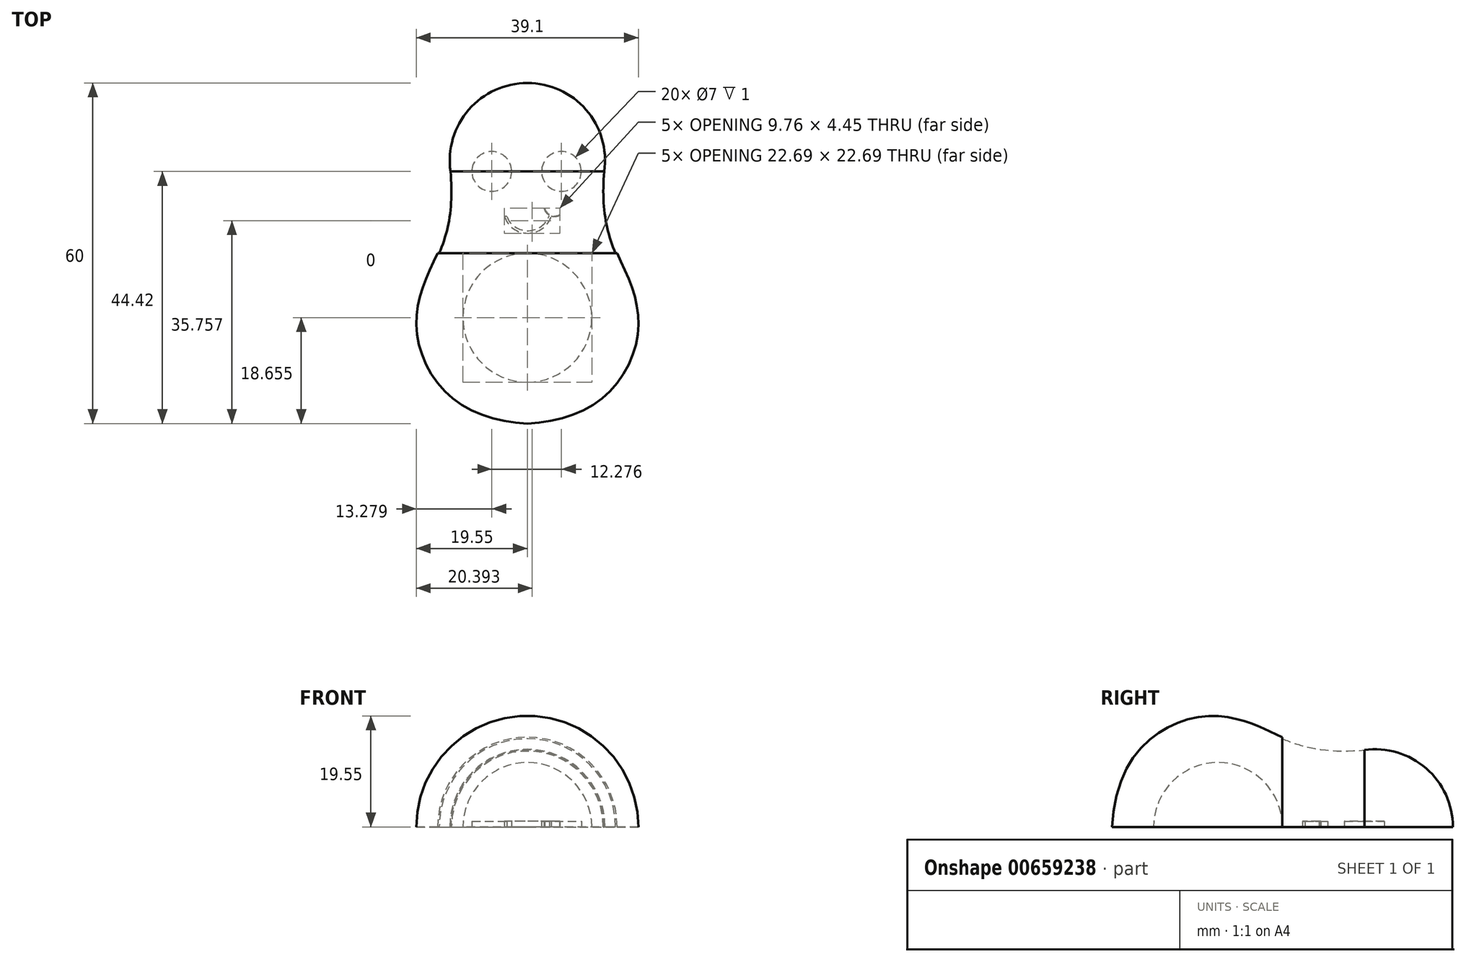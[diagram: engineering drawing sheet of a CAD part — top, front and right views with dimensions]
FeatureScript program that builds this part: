
annotation { "Feature Type Name" : "Feature", "Feature Type Description" : "" }
export const myFeature = defineFeature(function(context is Context, id is Id, definition is map)
    precondition{}
    {
        {
            var Q0;
            Q0=qCreatedBy(makeId("Top.planeOp"),FACE);
            var sketch = newSketch(context, id + "F0", { "sketchPlane" : qUnion([Q0])});
            skArc(sketch, "E0", {"start": v(13.54, 0) * mm, "mid": v(0, 15.58) * mm, "end": v(-13.54, 0) * mm});
            skFitSpline(sketch, "E1", {"points": [v(13.54, 0) * mm, v(14.1, -9.9) * mm, v(17.71, -18.6) * mm, v(19.44, -28.62) * mm, v(13.54, -39.68) * mm, v(0, -44.42) * mm, v(-13.72, -40.7) * mm, v(-20.09, -28.62) * mm, v(-17.3, -18.38) * mm, v(-14.11, -10.2) * mm, v(-13.54, 0) * mm], "startDerivative": vector(5.18, -120.5) * mm, "endDerivative": vector(-10.42, 118.7) * mm});
            skLineSegment(sketch, "E2", {"start": v(0, 15.58) * mm, "end": v(0, -44.42) * mm});
            skArc(sketch, "E3", {"start": v(0, -37.1) * mm, "mid": v(11.34, -25.77) * mm, "end": v(0, -14.42) * mm});
            skLineSegment(sketch, "E4", {"start": v(15.8, -14.42) * mm, "end": v(-15.53, -14.42) * mm});
            skLineSegment(sketch, "E5", {"start": v(0, -14.42) * mm, "end": v(0, -44.42) * mm});
            skLineSegment(sketch, "E6", {"start": v(0, 15.58) * mm, "end": v(0, -14.42) * mm});
            skSolve(sketch);
        }
        {
            var Q0;
            {var subQ3=sQuery(id+"F0.wireOp",EDGE,"E3");Q0=makeQuery(id+"F0.imprint","IMPRINT",FACE,{"disambiguationData":[TD([[makeQuery(id+"F0.imprint","IMPRINT",EDGE,{"derivedFrom":subQ3}),-1.0]])]});}
            var Q1;
            {var subQ0=sQuery(id+"F0.wireOp",EDGE,"E3");var subQ1=sQuery(id+"F0.wireOp",EDGE,"E2");var subQ2=makeQuery(id+"F0.imprint","INTERSECT",VERTEX,{"derivedFrom":[subQ1,subQ0]});Q1=makeQuery(id+"F0.imprint","IMPRINT",FACE,{"disambiguationData":[TD([[makeQuery(id+"F0.imprint","IMPRINT",EDGE,{"disambiguationData":[TD([[subQ2,-1.0]])],"derivedFrom":subQ0}),1.0]])]});}
            var Q2;
            Q2=sQuery(id+"F0.wireOp",EDGE,"E2");
            revolve(context, id + "F1", {"entities" : qUnion([Q0, Q1]), "axis" : qUnion([Q2]), "revolveType" : RevolveType.ONE_DIRECTION, "angle" : 180 * degree});
        }
        {
            var Q0;
            {var subQ0=sQuery(id+"F0.wireOp",EDGE,"E1");var subQ1=sQuery(id+"F0.wireOp",EDGE,"E0");var subQ2=makeQuery(id+"F0.imprint","INTERSECT",VERTEX,{"disambiguationData":[OD(1.0)],"derivedFrom":[subQ1,subQ0]});Q0=makeQuery(id+"F0.imprint","IMPRINT",FACE,{"disambiguationData":[TD([[makeQuery(id+"F0.imprint","IMPRINT",EDGE,{"disambiguationData":[TD([[subQ2,1.0]])],"derivedFrom":subQ1}),1.0]])]});}
            var Q1;
            Q1=sQuery(id+"F0.wireOp",EDGE,"E2");
            revolve(context, id + "F2", {"entities" : qUnion([Q0]), "axis" : qUnion([Q1]), "revolveType" : RevolveType.ONE_DIRECTION, "oppositeDirection" : true, "angle" : 180 * degree});
        }
        {
            var Q0;
            {var subQ0=sQuery(id+"F0.wireOp",EDGE,"E3");var subQ1=sQuery(id+"F0.wireOp",EDGE,"E2");var subQ2=makeQuery(id+"F0.imprint","INTERSECT",VERTEX,{"derivedFrom":[subQ1,subQ0]});Q0=makeQuery(id+"F0.imprint","IMPRINT",FACE,{"disambiguationData":[TD([[makeQuery(id+"F0.imprint","IMPRINT",EDGE,{"disambiguationData":[TD([[subQ2,-1.0]])],"derivedFrom":subQ0}),1.0]])]});}
            var Q1;
            Q1=sQuery(id+"F0.wireOp",EDGE,"E2");
            revolve(context, id + "F3", {"operationType" : NewBodyOperationType.REMOVE, "entities" : qUnion([Q0]), "axis" : qUnion([Q1]), "revolveType" : RevolveType.ONE_DIRECTION, "angle" : 180 * degree});
        }
        {
            var Q0;
            Q0=makeQuery(id+"F2.opRevolve","CAP_FACE",FACE,{"disambiguationData":[OSD([sQuery(id+"F0.wireOp",EDGE,"E0"),sQuery(id+"F0.wireOp",EDGE,"E1"),sQuery(id+"F0.wireOp",EDGE,"E2"),sQuery(id+"F0.wireOp",EDGE,"E4")])],"isStart":false});
            var sketch = newSketch(context, id + "F4", { "sketchPlane" : qUnion([Q0])});
            skCircle(sketch, "E7", {"center": v(-6.27, 0) * mm, "radius": 3.5 * mm});
            skCircle(sketch, "E8", {"center": v(6, 0) * mm, "radius": 3.5 * mm});
            skArc(sketch, "E9", {"start": v(3.87, 7.71) * mm, "mid": v(0.2, 10.44) * mm, "end": v(-3.64, 7.92) * mm});
            skArc(sketch, "E10", {"start": v(5.72, 7.71) * mm, "mid": v(4, 7.78) * mm, "end": v(2.93, 6.44) * mm});
            skArc(sketch, "E11", {"start": v(4.23, 7.86) * mm, "mid": v(0.12, 10.89) * mm, "end": v(-4.04, 7.92) * mm});
            skLineSegment(sketch, "E12", {"start": v(-3.64, 7.92) * mm, "end": v(-4.04, 7.92) * mm});
            skArc(sketch, "E13", {"start": v(5.67, 7.63) * mm, "mid": v(4.06, 7.68) * mm, "end": v(3.04, 6.44) * mm});
            skLineSegment(sketch, "E14", {"start": v(5.67, 7.63) * mm, "end": v(5.72, 7.71) * mm});
            skLineSegment(sketch, "E15", {"start": v(2.93, 6.44) * mm, "end": v(3.04, 6.44) * mm});
            skSolve(sketch);
        }
        {
            var Q0;
            Q0=makeQuery(id+"F4.imprint","IMPRINT",FACE,{"disambiguationData":[TD([[makeQuery(id+"F4.imprint","IMPRINT",EDGE,{"derivedFrom":sQuery(id+"F4.wireOp",EDGE,"E8")}),1.0]])]});
            var Q1;
            Q1=makeQuery(id+"F4.imprint","IMPRINT",FACE,{"disambiguationData":[TD([[makeQuery(id+"F4.imprint","IMPRINT",EDGE,{"derivedFrom":sQuery(id+"F4.wireOp",EDGE,"E7")}),1.0]])]});
            extrude(context, id + "F5", {"entities" : qUnion([Q0, Q1]), "operationType" : NewBodyOperationType.REMOVE, "oppositeDirection" : true, "depth" : 1 * mm, "offsetDistance" : 25 * mm});
        }
        {
            var Q0;
            Q0=makeQuery(id+"F4.imprint","IMPRINT",FACE,{"disambiguationData":[TD([[makeQuery(id+"F4.imprint","IMPRINT",EDGE,{"derivedFrom":sQuery(id+"F4.wireOp",EDGE,"E13")}),-1.0]])]});
            var Q1;
            {var subQ0=sQuery(id+"F4.wireOp",EDGE,"E9");Q1=makeQuery(id+"F4.imprint","IMPRINT",FACE,{"disambiguationData":[TD([[makeQuery(id+"F4.imprint","IMPRINT",EDGE,{"derivedFrom":subQ0}),-1.0]])]});}
            extrude(context, id + "F6", {"entities" : qUnion([Q0, Q1]), "operationType" : NewBodyOperationType.REMOVE, "oppositeDirection" : true, "depth" : 1 * mm, "offsetDistance" : 25 * mm});
        }
    });
